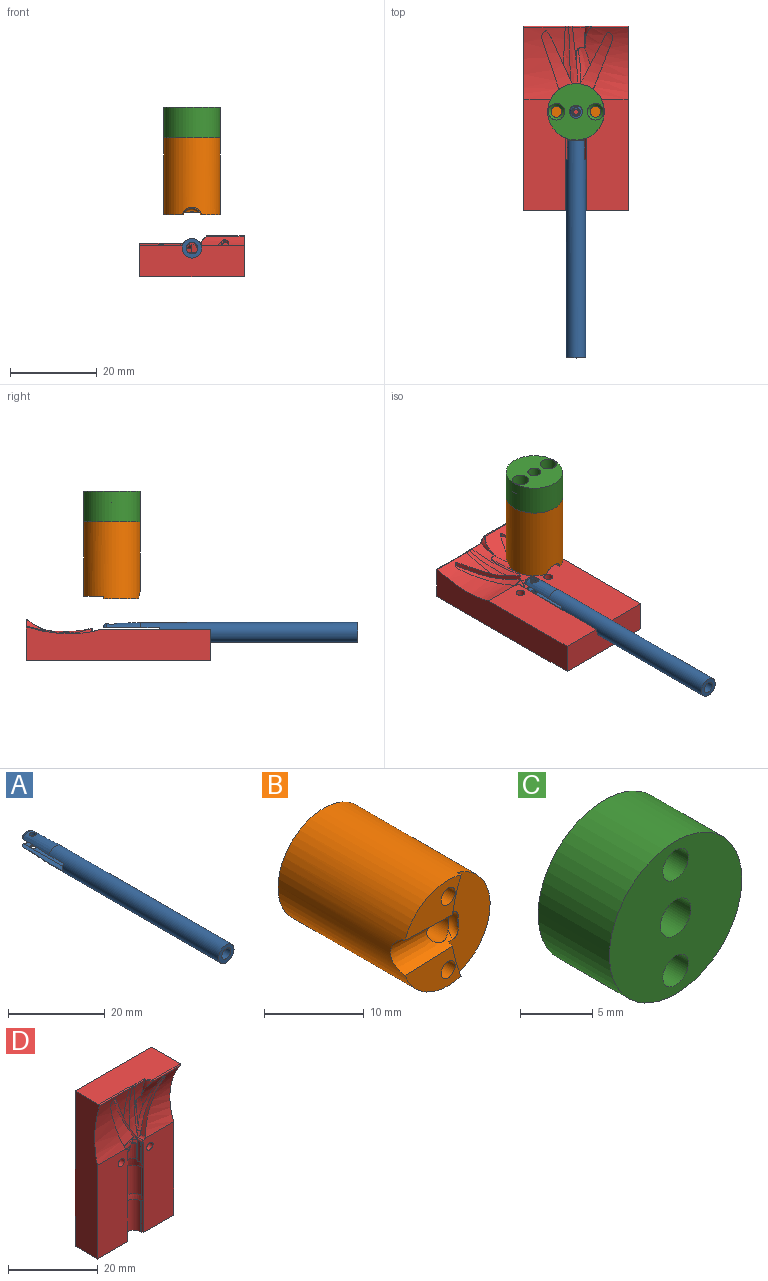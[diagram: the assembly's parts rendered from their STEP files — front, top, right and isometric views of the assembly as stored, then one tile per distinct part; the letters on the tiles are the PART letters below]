
ASSEMBLY  parts=4 mates=3
PART A: 17 faces, bbox 4.5x58.6x4.5 mm
  f0: cylinder r=1mm len=2mm, axis (0,0,1), area 2.1mm2, adj f8,f13
  f1: plane 12.91x1.2mm, normal (0,0,1), area 13.7mm2, adj f6,f8,f9,f11,f16
  f2: plane 12.91x1.2mm, normal (0,0,1), area 13.7mm2, adj f3,f6,f8,f11,f16
  f3: plane 2x1.42mm, normal (0,1,0), area 2mm2, adj f2,f6,f10,f11
  f4: plane 12.91x1.2mm, normal (0,0,-1), area 13.7mm2, adj f5,f6,f9,f11,f15
  f5: cone r=2.25mm half-angle=1.9deg, axis (0,-1,0), area 34.4mm2, adj f4,f6,f10,f14,f15
  f6: cylinder r=2.25mm len=50mm, axis (0,1,0), area 689.1mm2, adj f1,f2,f3,f4,f5,f7,f8,f9
  f7: plane 4.5x4.5mm, normal (0,-1,0), area 10.6mm2, adj f6,f11
  f8: cone r=2.25mm half-angle=1.9deg, axis (0,-1,0), area 32.7mm2, adj f0,f1,f2,f6,f16
  f9: plane 2x1.42mm, normal (0,1,0), area 2mm2, adj f1,f4,f6,f11
  f10: plane 12.91x1.2mm, normal (0,0,-1), area 13.7mm2, adj f3,f5,f6,f11,f15
  f11: cylinder r=1.3mm len=58.61mm, axis (0,1,0), area 416.7mm2, adj f1,f2,f3,f4,f7,f9,f10,f12
  f12: cylinder r=0.7mm len=1.4mm, axis (0,0,1), area 1.6mm2, adj f11,f13
  f13: plane 2x2mm, normal (0,0,-1), area 1.6mm2, adj f0,f12
  f14: cylinder r=0.7mm len=1.4mm, axis (0,0,-1), area 3.4mm2, adj f5,f11
  f15: torus R=1.23mm, axis (0,1,0), area 3.6mm2, adj f4,f5,f10,f11
  f16: torus R=1.23mm, axis (0,1,0), area 3.6mm2, adj f1,f2,f8,f11
PART B: 23 faces, bbox 13.5x18.3x13.5 mm
  f0: plane 1.12x0.13mm, normal (-1,0,0), area 0.1mm2, adj f1,f10
  f1: torus R=1.23mm, axis (1,0,0), area 2.7mm2, adj f0,f4,f10,f11
  f2: plane 7.99x4.58mm, normal (0,-1,0), area 22.1mm2, adj f3,f4,f7,f8
  f3: cylinder r=6.5mm len=17.66mm, axis (0,-1,0), area 706.4mm2, adj f2,f4,f5,f8,f9,f10,f15
  f4: cone r=2.25mm half-angle=1.9deg, axis (-1,0,0), area 33.8mm2, adj f1,f2,f3,f5,f8,f9,f10,f11
  f5: plane 7.99x4.58mm, normal (0,-1,0), area 22.1mm2, adj f3,f4,f6,f9
  f6: cylinder r=1mm len=9.66mm, axis (0,-1,0), area 60.7mm2, adj f5,f17
  f7: cylinder r=1mm len=9.66mm, axis (0,-1,0), area 60.7mm2, adj f2,f18
  f8: cylinder r=15mm len=4.55mm, axis (0,-1,0), area 2.5mm2, adj f2,f3,f4,f10
  f9: cylinder r=15mm len=4.55mm, axis (0,-1,0), area 2.5mm2, adj f3,f4,f5,f10
  f10: plane 12.95x6.39mm, normal (0,-1,0), area 49.4mm2, adj f0,f1,f3,f4,f8,f9
  f11: cylinder r=1.5mm len=3.39mm, axis (0,1,0), area 31.9mm2, adj f1,f4,f13
  f12: plane 5.01x5.01mm, normal (0,1,0), area 12.1mm2, adj f14,f16
  f13: extruded ~5x3mm, area 47.1mm2, adj f11,f14
  f14: plane 3.11x3.11mm, normal (0,1,0), area 0.5mm2, adj f12,f13
  f15: plane 13x13mm, normal (0,1,0), area 103.3mm2, adj f3,f16,f19,f21
  f16: cylinder r=2.5mm len=8mm, axis (0,-1,0), area 125.7mm2, adj f12,f15
  f17: plane 2x2mm, normal (0,-1,0), area 3.1mm2, adj f6
  f18: plane 2x2mm, normal (0,-1,0), area 3.1mm2, adj f7
  f19: cylinder r=1.25mm len=7mm, axis (0,-1,0), area 55mm2, adj f15,f20
  f20: plane 2.5x2.5mm, normal (0,1,0), area 4.9mm2, adj f19
  f21: cylinder r=1.25mm len=7mm, axis (0,-1,0), area 55mm2, adj f15,f22
  f22: plane 2.5x2.5mm, normal (0,1,0), area 4.9mm2, adj f21
PART C: 10 faces, bbox 13x7x13 mm
  f0: cylinder r=1.25mm len=3.7mm, axis (0,-1,0), area 29.1mm2, adj f5,f8
  f1: cylinder r=1.25mm len=3.7mm, axis (0,-1,0), area 29.1mm2, adj f5,f9
  f2: cylinder r=6.5mm len=13mm, axis (0,-1,0), area 285.9mm2, adj f4,f5
  f3: cylinder r=1.5mm len=7mm, axis (0,-1,0), area 66mm2, adj f4,f5
  f4: plane 13x13mm, normal (0,1,0), area 103mm2, adj f2,f3,f6,f7
  f5: plane 13x13mm, normal (0,-1,0), area 115.8mm2, adj f0,f1,f2,f3
  f6: cylinder r=1.9mm len=3.8mm, axis (0,1,0), area 31.6mm2, adj f4,f9
  f7: cylinder r=1.9mm len=3.8mm, axis (0,1,0), area 31.6mm2, adj f4,f8
  f8: cone r=1.25mm half-angle=45deg, axis (0,1,0), area 9.1mm2, adj f0,f7
  f9: cone r=1.25mm half-angle=45deg, axis (0,1,0), area 9.1mm2, adj f1,f6
PART D: 122 faces, bbox 24.4x10x43.9 mm
  f0: plane 5.63x0.18mm, normal (-1,0,0), area 1mm2, adj f1,f119,f120,f121
  f1: plane 1.32x0.32mm, normal (0,0,-1), area 0.2mm2, adj f0,f2,f3,f116,f119,f121
  f2: plane 6.77x0.06mm, normal (-0.71,-0.71,0), area 0.5mm2, adj f1,f116,f119,f120
  f3: cylinder r=3.09mm len=1.58mm, axis (0,-1,0), area 0.1mm2, adj f1,f4,f114,f115,f116
  f4: cylinder r=0.41mm len=1.59mm, axis (0,-1,0), area 1.1mm2, adj f3,f5,f113,f114,f116
  f5: cylinder r=10.3mm len=4.14mm, axis (0.92,0,-0.39), area 7.1mm2, adj f4,f6,f110,f111,f112,f113,f114
  f6: plane 13.18x5.14mm, normal (-0.93,0,0.36), area 12.4mm2, adj f5,f7,f17,f18,f112,f113
  f7: cylinder r=22.66mm len=14.99mm, axis (0.92,0,-0.39), area 39.1mm2, adj f6,f8,f13,f14,f15,f16,f17,f111
  f8: plane 0.72x0.23mm, normal (-0.11,0,-0.99), area 0.1mm2, adj f7,f9,f12,f13,f17
  f9: cylinder r=0.21mm len=0.14mm, axis (-0.59,-0.8,0.08), area 0mm2, adj f8,f10,f11,f12,f13
  f10: plane 0.15x0.1mm, normal (-0.11,0,-0.99), area 0mm2, adj f9,f11,f17,f18
  f11: cylinder r=0.21mm len=0.24mm, axis (-0.58,-0.81,0.06), area 0mm2, adj f9,f10,f13,f14,f18
  f12: bspline ~0.46x0.36mm, area 0mm2, adj f8,f9
  f13: plane 0.77x0.08mm, normal (-0.25,0,-0.97), area 0.1mm2, adj f7,f8,f9,f11,f14
  f14: extruded ~0.84x0.2mm, area 0.2mm2, adj f7,f11,f13,f15,f18
  f15: cylinder r=3.63mm len=1.25mm, axis (0,-1,0), area 0.7mm2, adj f7,f14,f16,f18
  f16: plane 6.02x3.14mm, normal (0.89,0,-0.46), area 5.7mm2, adj f7,f15,f18,f111
  f17: cylinder r=1.54mm len=1.92mm, axis (0,-1,0), area 1.1mm2, adj f6,f7,f8,f10,f18
  f18: extruded ~16.56x10.43mm, area 130.4mm2, adj f6,f10,f11,f14,f15,f16,f17,f19
  f19: plane 42.41x9.38mm, normal (1,0,0), area 295.6mm2, adj f18,f20,f91,f104,f105,f116
  f20: plane 24x9.18mm, normal (0,0,1), area 196.1mm2, adj f19,f21,f26,f87,f88,f89,f90,f91
  f21: cylinder r=0.2mm len=3.11mm, axis (-1,0,0), area 1.1mm2, adj f20,f22,f26,f90,f108
  f22: cylinder r=2.66mm len=4.15mm, axis (0,0,-1), area 3.3mm2, adj f21,f23,f24,f90,f106,f108
  f23: plane 0.21x0.03mm, normal (-1,0,0), area 0mm2, adj f22,f107,f108
  f24: bspline ~0.17x0.13mm, area 0mm2, adj f22,f25,f105,f106
  f25: bspline ~0.25x0.2mm, area 0mm2, adj f24,f90,f105
  f26: bspline ~2.19x0.63mm, area 0.3mm2, adj f20,f21,f27,f87
  f27: bspline ~16.63x2.69mm, area 18.9mm2, adj f26,f28,f29,f85,f86,f108,f111
  f28: bspline ~12.03x2.78mm, area 5.9mm2, adj f27,f108,f109,f111
  f29: plane 0.99x0.03mm, normal (-0.91,0,-0.41), area 0mm2, adj f27,f30,f85,f111
  f30: cylinder r=2.02mm len=3.4mm, axis (0.94,0,0.34), area 1mm2, adj f29,f31,f78,f79,f80,f81,f82,f83
  f31: cylinder r=1.03mm len=0.75mm, axis (0,-1,0), area 0.6mm2, adj f30,f32,f39,f75,f77,f78,f84
  f32: extruded ~16.55x9.5mm, area 123.3mm2, adj f31,f33,f34,f35,f36,f37,f38,f39
  f33: cylinder r=1.54mm len=1.78mm, axis (0,-1,0), area 1.8mm2, adj f32,f34,f78,f80
  f34: cylinder r=1.04mm len=0.87mm, axis (0,-1,0), area 0.1mm2, adj f32,f33,f35,f80
  f35: cylinder r=2.54mm len=0.88mm, axis (0,-1,0), area 0.1mm2, adj f32,f34,f36,f80
  f36: extruded ~0.9x0.19mm, area 0.2mm2, adj f32,f35,f37,f80
  f37: cylinder r=0.16mm len=0.92mm, axis (0,1,0), area 0.1mm2, adj f32,f36,f38,f80
  f38: cylinder r=15.98mm len=2.6mm, axis (0,-1,0), area 3.1mm2, adj f32,f37,f80,f85
  f39: plane 25.6x9.78mm, normal (0,-1,0), area 241mm2, adj f31,f32,f40,f67,f68,f69,f70,f71
  f40: plane 0.53x0.09mm, normal (1,0,-0.08), area 0mm2, adj f39,f41,f42,f66,f67,f75,f84
  f41: cylinder r=0.41mm len=0.14mm, axis (0,-1,0), area 0mm2, adj f40,f75,f77,f84
  f42: cylinder r=139.81mm len=1.59mm, axis (0.94,0,0.34), area 0.5mm2, adj f40,f43,f63,f65,f67,f83,f84
  f43: plane 1.05x0.91mm, normal (0,0,-1), area 0.9mm2, adj f42,f44,f46,f63,f81,f83,f110,f114
  f44: plane 0.23x0.12mm, normal (0,1,0), area 0mm2, adj f43,f45,f81,f83
  f45: cylinder r=5.15mm len=0.17mm, axis (-0.92,0,0.39), area 0mm2, adj f44,f81,f82,f83
  f46: cylinder r=2.25mm len=5.63mm, axis (0,0,1), area 5.8mm2, adj f43,f47,f63,f114
  f47: cone r=2.1mm half-angle=10deg, axis (0,0,-1), area 14.2mm2, adj f46,f48,f58,f69,f114,f120,f121
  f48: cylinder r=2.5mm len=7.74mm, axis (0,0,-1), area 60.8mm2, adj f47,f49,f57,f70
  f49: cone r=2.5mm half-angle=10deg, axis (0,0,1), area 10.7mm2, adj f48,f50,f54,f71
  f50: plane 1.42x0.58mm, normal (-0.98,0,0.17), area 0.6mm2, adj f49,f51,f52,f53,f57,f116
  f51: plane 9.54x0.06mm, normal (-0.71,-0.71,0), area 0.8mm2, adj f50,f52,f104,f116
  f52: plane 9.2x0.34mm, normal (-0.92,-0.38,0), area 3.3mm2, adj f50,f51,f53,f104
  f53: plane 8.4x0.18mm, normal (-1,0,0), area 1.5mm2, adj f50,f52,f54,f104
  f54: cylinder r=2.25mm len=8.4mm, axis (0,0,1), area 59.4mm2, adj f49,f53,f55,f104
  f55: plane 8.4x0.18mm, normal (1,0,0), area 1.5mm2, adj f54,f56,f71,f104
  f56: plane 9.2x0.34mm, normal (0.92,-0.38,0), area 3.3mm2, adj f55,f71,f72,f104
  f57: plane 7.74x0.58mm, normal (-1,0,0), area 4.5mm2, adj f48,f50,f116,f120
  f58: cone r=1.98mm half-angle=1.9deg, axis (0,0,-1), area 17.2mm2, adj f47,f59,f61,f114
  f59: torus R=1.23mm, axis (0,0,1), area 3.3mm2, adj f58,f60,f114
  f60: plane 1.44x0.23mm, normal (0,0,-1), area 0.2mm2, adj f59,f114
  f61: cylinder r=0.6mm len=1.2mm, axis (0,-1,0), area 4mm2, adj f58,f62
  f62: plane 1.2x1.2mm, normal (0,-1,0), area 1.1mm2, adj f61
  f63: plane 5.8x0.18mm, normal (1,0,0), area 1mm2, adj f42,f43,f46,f64,f65,f69
  f64: plane 6.6x0.35mm, normal (0.92,-0.38,0), area 2.2mm2, adj f63,f67,f68,f69
  f65: plane 0.1x0.02mm, normal (0.96,0,-0.28), area 0mm2, adj f42,f63,f67
  f66: bspline ~0.15x0.1mm, area 0mm2, adj f40,f67
  f67: cylinder r=0.41mm len=0.53mm, axis (0,-1,0), area 0.1mm2, adj f39,f40,f42,f64,f65,f66,f68
  f68: plane 6.74x0.06mm, normal (0.71,-0.71,0), area 0.5mm2, adj f39,f64,f67,f69
  f69: plane 1.42x0.58mm, normal (0.98,0,-0.17), area 0.6mm2, adj f39,f47,f63,f64,f68,f70
  f70: plane 7.74x0.58mm, normal (1,0,0), area 4.5mm2, adj f39,f48,f69,f71
  f71: plane 1.42x0.58mm, normal (0.98,0,0.17), area 0.6mm2, adj f39,f49,f55,f56,f70,f72
  f72: plane 9.54x0.06mm, normal (0.71,-0.71,0), area 0.8mm2, adj f39,f56,f71,f104
  f73: cylinder r=1mm len=5mm, axis (0,-1,0), area 31.4mm2, adj f39,f74
  f74: plane 2x2mm, normal (0,-1,0), area 3.1mm2, adj f73
  f75: cylinder r=0.41mm len=0.44mm, axis (0,-1,0), area 0.3mm2, adj f31,f39,f40,f41,f76
  f76: bspline ~0.41x0.34mm, area 0mm2, adj f75,f77
  f77: cylinder r=0.4mm len=0.3mm, axis (0,-1,0), area 0mm2, adj f31,f41,f76,f84
  f78: plane 13.41x4.52mm, normal (0.95,0,0.32), area 13.1mm2, adj f30,f31,f32,f33,f80
  f79: plane 0.1x0.04mm, normal (0.34,0,-0.94), area 0mm2, adj f30,f80
  f80: cylinder r=23.18mm len=15.86mm, axis (0.94,0,0.34), area 42.2mm2, adj f30,f33,f34,f35,f36,f37,f38,f78
  f81: cone r=181.1mm half-angle=55deg, axis (0.89,0,-0.46), area 0mm2, adj f30,f43,f44,f45,f82,f110
  f82: cylinder r=178.84mm len=2.23mm, axis (0.92,0,-0.39), area 0mm2, adj f30,f45,f81,f83
  f83: plane 2.48x1.28mm, normal (0.89,0,-0.46), area 0.2mm2, adj f30,f42,f43,f44,f45,f82,f84
  f84: cylinder r=5.29mm len=3.43mm, axis (0.94,0,0.34), area 2.6mm2, adj f30,f31,f40,f41,f42,f77,f83
  f85: plane 11.56x5.33mm, normal (-0.91,0,-0.41), area 13.5mm2, adj f27,f29,f32,f38,f80,f86
  f86: bspline ~14.37x2.02mm, area 13.2mm2, adj f27,f32,f85,f87
  f87: bspline ~3.07x0.64mm, area 0.3mm2, adj f20,f26,f86,f88
  f88: cylinder r=0.2mm len=9.5mm, axis (-1,0,0), area 3.6mm2, adj f20,f32,f87,f89
  f89: plane 42.41x7.7mm, normal (-1,0,0), area 292.5mm2, adj f20,f32,f39,f88,f91,f104
  f90: torus R=2.46mm, axis (0,0,-1), area 0.7mm2, adj f20,f21,f22,f25
  f91: plane 42.41x24mm, normal (0,1,0), area 938.7mm2, adj f19,f20,f89,f92,f94,f96,f98,f100
  f92: cylinder r=2.05mm len=5.2mm, axis (0,1,0), area 67mm2, adj f91,f93
  f93: plane 4.1x4.1mm, normal (0,1,0), area 13.2mm2, adj f92
  f94: cylinder r=2.05mm len=4.5mm, axis (0,1,0), area 58mm2, adj f91,f95
  f95: plane 4.1x4.1mm, normal (0,1,0), area 13.2mm2, adj f94
  f96: cylinder r=2.05mm len=4.1mm, axis (0,1,0), area 52.8mm2, adj f91,f97
  f97: plane 4.1x4.1mm, normal (0,1,0), area 13.2mm2, adj f96
  f98: cylinder r=2.05mm len=4.6mm, axis (0,1,0), area 59.3mm2, adj f91,f99
  f99: plane 4.1x4.1mm, normal (0,1,0), area 13.2mm2, adj f98
  f100: cylinder r=2.05mm len=4.1mm, axis (0,1,0), area 52.8mm2, adj f91,f101
  f101: plane 4.1x4.1mm, normal (0,1,0), area 13.2mm2, adj f100
  f102: cylinder r=2.05mm len=4.1mm, axis (0,1,0), area 52.8mm2, adj f91,f103
  f103: plane 4.1x4.1mm, normal (0,1,0), area 13.2mm2, adj f102
  f104: plane 24x7.09mm, normal (0,0,-1), area 159.6mm2, adj f19,f39,f51,f52,f53,f54,f55,f56
  f105: cylinder r=0.2mm len=8.51mm, axis (1,0,0), area 3.8mm2, adj f18,f19,f20,f24,f25
  f106: bspline ~5.96x3.09mm, area 0.6mm2, adj f18,f22,f24,f107
  f107: bspline ~3.22x1.32mm, area 0mm2, adj f18,f23,f106,f108
  f108: extruded ~9.32x2.96mm, area 13.8mm2, adj f18,f21,f22,f23,f27,f28,f107,f109
  f109: bspline ~9.55x3.81mm, area 13.4mm2, adj f18,f28,f108,f111
  f110: plane 2.59x1.34mm, normal (0.89,0,-0.46), area 2.8mm2, adj f5,f30,f43,f81,f111,f114
  f111: plane 7.29x3.94mm, normal (0.89,0,-0.46), area 10.8mm2, adj f5,f7,f16,f18,f27,f28,f29,f109
  f112: plane 3.14x1.33mm, normal (-0.39,0,-0.92), area 0mm2, adj f5,f6,f7,f111
  f113: cylinder r=1.03mm len=1.66mm, axis (0,-1,0), area 1.7mm2, adj f4,f5,f6,f18,f116
  f114: plane 7.44x4.54mm, normal (0,-1,0), area 5.5mm2, adj f3,f4,f5,f43,f46,f47,f58,f59
  f115: plane 0.26x0.11mm, normal (0,0,1), area 0mm2, adj f3,f114,f121
  f116: plane 25.53x9.91mm, normal (0,-1,0), area 240.3mm2, adj f1,f2,f3,f4,f18,f19,f50,f51
  f117: cylinder r=1mm len=5.6mm, axis (0,-1,0), area 35.2mm2, adj f116,f118
  f118: plane 2x2mm, normal (0,-1,0), area 3.1mm2, adj f117
  f119: plane 6.43x0.34mm, normal (-0.92,-0.38,0), area 2.2mm2, adj f0,f1,f2,f120
  f120: plane 1.42x0.58mm, normal (-0.98,0,-0.17), area 0.6mm2, adj f0,f2,f47,f57,f116,f119
  f121: cylinder r=2.25mm len=5.63mm, axis (0,0,1), area 5.8mm2, adj f0,f1,f47,f114,f115
PLACE A rot(axis=(0,1,0),180deg) t=(-10.11,-20.25,9.49)mm
PLACE B rot(axis=(0.58,0.58,0.58),120deg) t=(-10.11,-13.63,18.57)mm
PLACE C rot(axis=(0.58,0.58,0.58),120deg) t=(-10.11,-13.63,18.57)mm
PLACE D rot(axis=(-1,0,0),90deg) t=(0,18.67,8.49)mm fixed
MATE fastened B.f21 <-> C.f1  axis (0,0,1) through (-5.61,-13.63,34.9)mm
MATE slider B.f3 <-> D.f61  axis (0,0,1) through (-10.11,-13.63,18.03)mm
MATE slider A.f15 <-> D.f47  axis (0,1,0) through (-10.11,-40.94,9.49)mm
